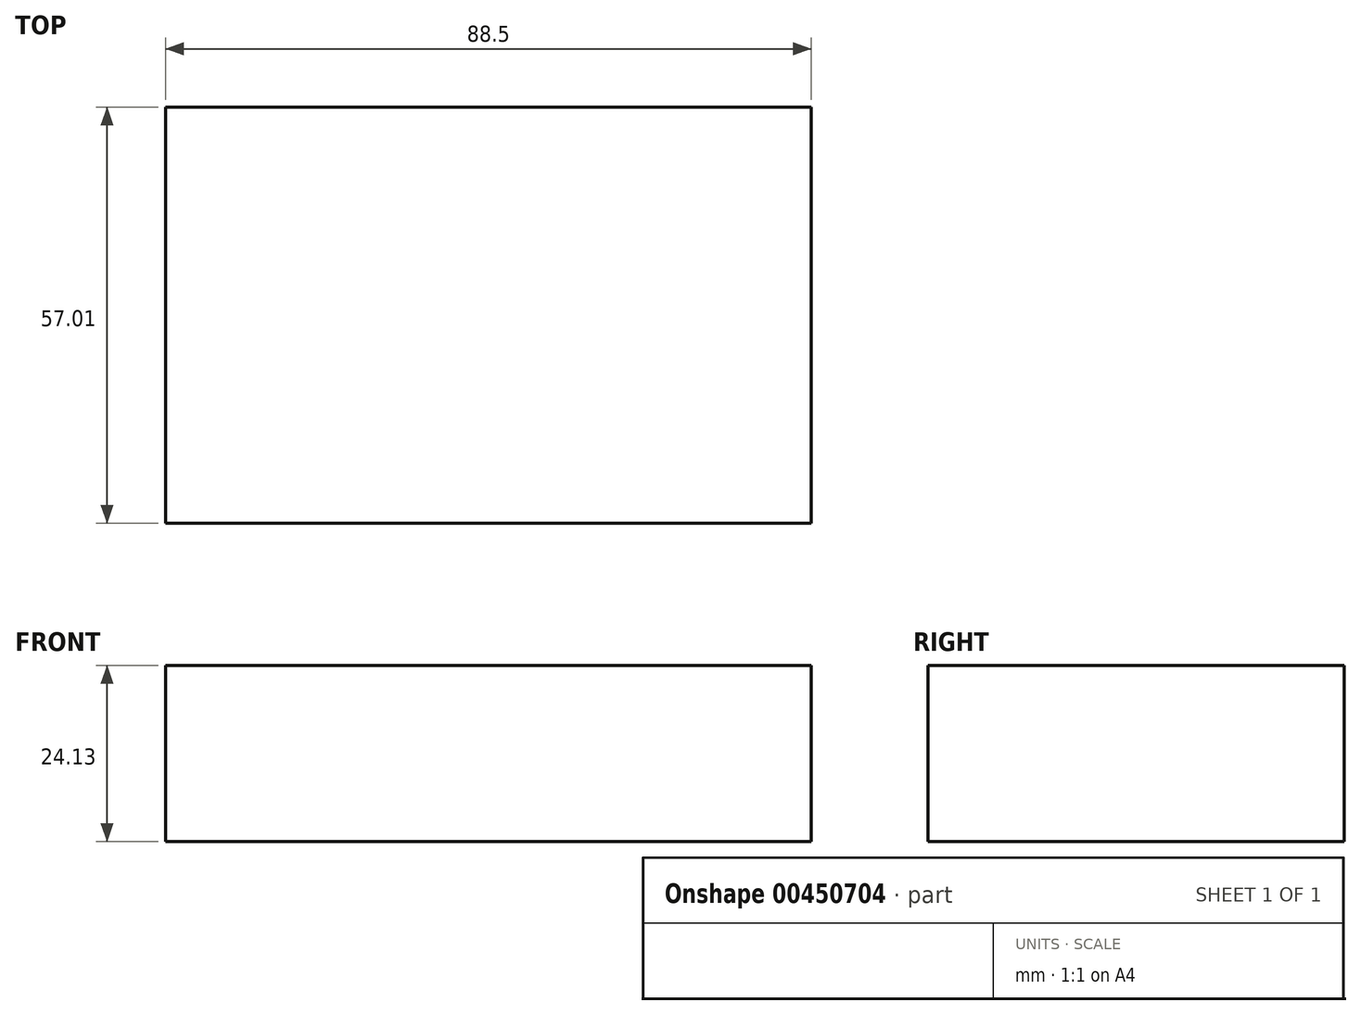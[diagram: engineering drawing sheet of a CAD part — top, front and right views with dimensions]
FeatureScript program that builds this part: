
annotation { "Feature Type Name" : "Feature", "Feature Type Description" : "" }
export const myFeature = defineFeature(function(context is Context, id is Id, definition is map)
    precondition{}
    {
        {
            var Q0;
            Q0=qCreatedBy(makeId("Top.planeOp"),FACE);
            var sketch = newSketch(context, id + "F0", { "sketchPlane" : qUnion([Q0])});
            skLineSegment(sketch, "E0", {"start": v(-68.87, -22.72) * mm, "end": v(19.63, -22.72) * mm});
            skLineSegment(sketch, "E1", {"start": v(19.63, -22.72) * mm, "end": v(19.63, 34.29) * mm});
            skLineSegment(sketch, "E2", {"start": v(19.63, 34.29) * mm, "end": v(-68.87, 34.29) * mm});
            skLineSegment(sketch, "E3", {"start": v(-68.87, 34.29) * mm, "end": v(-68.87, -22.72) * mm});
            skSolve(sketch);
        }
        {
            var Q0;
            Q0 = qSketchRegion(id + "F0", true);
            extrude(context, id + "F1", {"entities" : qUnion([Q0]), "depth" : 24.13 * mm});
        }
    });
